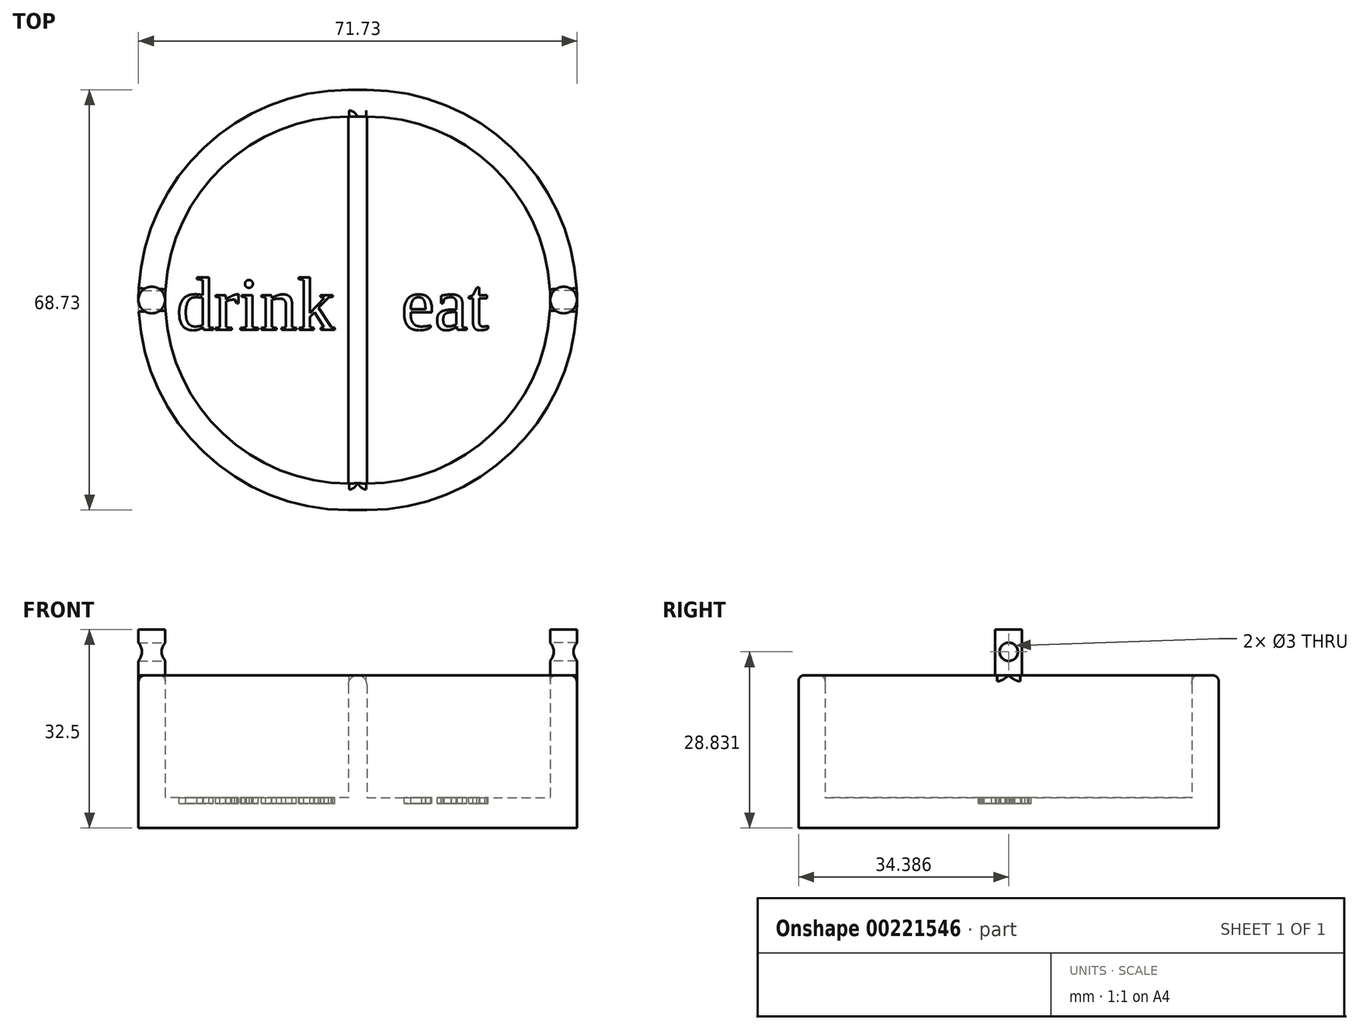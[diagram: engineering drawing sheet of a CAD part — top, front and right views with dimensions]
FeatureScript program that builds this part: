
annotation { "Feature Type Name" : "Feature", "Feature Type Description" : "" }
export const myFeature = defineFeature(function(context is Context, id is Id, definition is map)
    precondition{}
    {
        {
            var Q0;
            Q0=qCreatedBy(makeId("Top.planeOp"),FACE);
            var sketch = newSketch(context, id + "F0", { "sketchPlane" : qUnion([Q0])});
            skArc(sketch, "E0", {"start": v(1.15, 26.83) * mm, "mid": v(-28.85, -3.17) * mm, "end": v(1.15, -33.17) * mm});
            skArc(sketch, "E1", {"start": v(4.15, -33.17) * mm, "mid": v(34.15, -3.17) * mm, "end": v(4.15, 26.83) * mm});
            skLineSegment(sketch, "E2", {"start": v(1.15, 26.83) * mm, "end": v(4.15, 26.83) * mm});
            skLineSegment(sketch, "E3", {"start": v(1.15, -33.17) * mm, "end": v(4.15, -33.17) * mm});
            skArc(sketch, "E4", {"start": v(1.15, 31.2) * mm, "mid": v(-33.21, -3.17) * mm, "end": v(1.15, -37.54) * mm});
            skArc(sketch, "E5", {"start": v(4.15, -37.54) * mm, "mid": v(38.52, -3.17) * mm, "end": v(4.15, 31.2) * mm});
            skLineSegment(sketch, "E6", {"start": v(1.15, 31.2) * mm, "end": v(4.15, 31.2) * mm});
            skLineSegment(sketch, "E7", {"start": v(4.15, -37.54) * mm, "end": v(1.15, -37.54) * mm});
            skSolve(sketch);
        }
        {
            var Q0;
            Q0=makeQuery(id+"F0.imprint","IMPRINT",FACE,{"disambiguationData":[TD([[makeQuery(id+"F0.imprint","IMPRINT",EDGE,{"derivedFrom":sQuery(id+"F0.wireOp",EDGE,"E0")}),1.0]])]});
            var sketch = newSketch(context, id + "F1", { "sketchPlane" : qUnion([Q0])});
            skLineSegment(sketch, "E8", {"start": v(4.15, 26.83) * mm, "end": v(4.15, -33.17) * mm});
            skLineSegment(sketch, "E9", {"start": v(1.15, 26.83) * mm, "end": v(1.15, -33.17) * mm});
            skSolve(sketch);
        }
        {
            var Q0;
            Q0=qCreatedBy(makeId("Top.planeOp"),FACE);
            var sketch = newSketch(context, id + "F2", { "sketchPlane" : qUnion([Q0])});
            skLineSegment(sketch, "E10", {"start": v(1.15, 26.83) * mm, "end": v(4.15, 26.83) * mm});
            skLineSegment(sketch, "E11", {"start": v(4.15, 26.83) * mm, "end": v(4.15, -33.17) * mm});
            skLineSegment(sketch, "E12", {"start": v(4.15, -33.17) * mm, "end": v(1.15, -33.17) * mm});
            skLineSegment(sketch, "E13", {"start": v(1.15, -33.17) * mm, "end": v(1.15, 26.83) * mm});
            skSolve(sketch);
        }
        {
            var Q0;
            Q0=makeQuery(id+"F0.imprint","IMPRINT",FACE,{"disambiguationData":[TD([[makeQuery(id+"F0.imprint","IMPRINT",EDGE,{"derivedFrom":sQuery(id+"F0.wireOp",EDGE,"E0")}),-1.0]])]});
            extrude(context, id + "F3", {"entities" : qUnion([Q0]), "depth" : 25 * mm});
        }
        {
            var Q0;
            Q0=makeQuery(id+"F1.imprint","IMPRINT",FACE,{"disambiguationData":[TD([[makeQuery(id+"F1.imprint","IMPRINT",EDGE,{"derivedFrom":sQuery(id+"F1.wireOp",EDGE,"E9")}),-1.0]])]});
            var Q1;
            Q1=makeQuery(id+"F1.imprint","IMPRINT",FACE,{"disambiguationData":[TD([[makeQuery(id+"F1.imprint","IMPRINT",EDGE,{"derivedFrom":sQuery(id+"F1.wireOp",EDGE,"E8")}),1.0]])]});
            extrude(context, id + "F4", {"entities" : qUnion([Q0, Q1]), "operationType" : NewBodyOperationType.ADD, "depth" : 5 * mm});
        }
        {
            var Q0;
            Q0=makeQuery(id+"F2.imprint","IMPRINT",FACE,{"disambiguationData":[TD([[makeQuery(id+"F2.imprint","IMPRINT",EDGE,{"derivedFrom":sQuery(id+"F2.wireOp",EDGE,"E10")}),-1.0]])]});
            extrude(context, id + "F5", {"entities" : qUnion([Q0]), "operationType" : NewBodyOperationType.ADD, "depth" : 25 * mm});
        }
        {
            var Q0;
            Q0=makeQuery(id+"F5.opExtrude","CAP_EDGE",EDGE,{"disambiguationData":[OSD([sQuery(id+"F2.wireOp",EDGE,"E11")])],"isStart":false});
            var Q1;
            Q1=makeQuery(id+"F5.opExtrude","CAP_EDGE",EDGE,{"disambiguationData":[OSD([sQuery(id+"F2.wireOp",EDGE,"E13")])],"isStart":false});
            fillet(context, id + "F6", {"entities" : qUnion([Q0, Q1]), "radius" : 1.5 * mm, "tangentPropagation" : true, "allowEdgeOverflow" : false});
        }
        {
            var Q0;
            Q0=makeQuery(id+"F4.opExtrude","CAP_FACE",FACE,{"disambiguationData":[OSD([sQuery(id+"F0.wireOp",EDGE,"E1"),sQuery(id+"F1.wireOp",EDGE,"E8")])],"isStart":false});
            var sketch = newSketch(context, id + "F7", { "sketchPlane" : qUnion([Q0])});
            skText(sketch, "E14", { "text": "drink", "fontName": "Tinos-Regular.ttf"});
            skText(sketch, "E15", { "text": "eat", "fontName": "Tinos-Regular.ttf"});
            const initialGuessF7  = {"E14": [-0.02699, -0.00802, 1, 0, 0.00884], "E15": [0.00976, -0.00802, 1, 0, 0.00884]};
            skSetInitialGuess(sketch, initialGuessF7);
            skSolve(sketch);
        }
        {
            var Q0;
            Q0 = qSketchRegion(id + "F7", true);
            extrude(context, id + "F8", {"entities" : qUnion([Q0]), "operationType" : NewBodyOperationType.REMOVE, "oppositeDirection" : true, "depth" : 1 * mm});
        }
        {
            var Q0;
            Q0=makeQuery(id+"F5.boolean.opBoolean","MERGE",FACE,{"derivedFrom":[makeQuery(id+"F3.opExtrude","CAP_FACE",FACE,{"disambiguationData":[OSD([sQuery(id+"F0.wireOp",EDGE,"E0"),sQuery(id+"F0.wireOp",EDGE,"E1"),sQuery(id+"F0.wireOp",EDGE,"E2"),sQuery(id+"F0.wireOp",EDGE,"E3"),sQuery(id+"F0.wireOp",EDGE,"E4"),sQuery(id+"F0.wireOp",EDGE,"E5"),sQuery(id+"F0.wireOp",EDGE,"E6"),sQuery(id+"F0.wireOp",EDGE,"E7")])],"isStart":false}),makeQuery(id+"F5.opExtrude","CAP_FACE",FACE,{"disambiguationData":[OSD([sQuery(id+"F2.wireOp",EDGE,"E10"),sQuery(id+"F2.wireOp",EDGE,"E11"),sQuery(id+"F2.wireOp",EDGE,"E12"),sQuery(id+"F2.wireOp",EDGE,"E13")])],"isStart":false})]});
            var sketch = newSketch(context, id + "F9", { "sketchPlane" : qUnion([Q0])});
            skCircle(sketch, "E16", {"center": v(-31.03, -3.17) * mm, "radius": 2.18 * mm});
            skCircle(sketch, "E17", {"center": v(36.34, -3.17) * mm, "radius": 2.18 * mm});
            skSolve(sketch);
        }
        {
            var Q0;
            {var subQ0=sQuery(id+"F9.wireOp",EDGE,"E16");var subQ1=makeQuery(id+"F9.imprint","INTERSECT",VERTEX,{"derivedFrom":[makeQuery(id+"F3.opExtrude","CAP_EDGE",EDGE,{"disambiguationData":[OSD([sQuery(id+"F0.wireOp",EDGE,"E4")])],"isStart":false}),subQ0]});Q0=makeQuery(id+"F9.imprint","IMPRINT",FACE,{"disambiguationData":[TD([[makeQuery(id+"F9.imprint","IMPRINT",EDGE,{"disambiguationData":[TD([[subQ1,1.0]])],"derivedFrom":subQ0}),1.0]])]});}
            var Q1;
            {var subQ0=sQuery(id+"F9.wireOp",EDGE,"E17");var subQ1=makeQuery(id+"F9.imprint","INTERSECT",VERTEX,{"derivedFrom":[makeQuery(id+"F3.opExtrude","CAP_EDGE",EDGE,{"disambiguationData":[OSD([sQuery(id+"F0.wireOp",EDGE,"E5")])],"isStart":false}),subQ0]});Q1=makeQuery(id+"F9.imprint","IMPRINT",FACE,{"disambiguationData":[TD([[makeQuery(id+"F9.imprint","IMPRINT",EDGE,{"disambiguationData":[TD([[subQ1,-1.0]])],"derivedFrom":subQ0}),1.0]])]});}
            extrude(context, id + "F10", {"entities" : qUnion([Q0, Q1]), "operationType" : NewBodyOperationType.ADD, "depth" : 7.5 * mm});
        }
        {
            var Q0;
            Q0=qCreatedBy(makeId("Right.planeOp"),FACE);
            var sketch = newSketch(context, id + "F11", { "sketchPlane" : qUnion([Q0])});
            skCircle(sketch, "E18", {"center": v(-3.15, 28.83) * mm, "radius": 1.5 * mm});
            skSolve(sketch);
        }
        {
            var Q0;
            Q0=makeQuery(id+"F11.imprint","IMPRINT",FACE,{"disambiguationData":[TD([[makeQuery(id+"F11.imprint","IMPRINT",EDGE,{"derivedFrom":sQuery(id+"F11.wireOp",EDGE,"E18")}),1.0]])]});
            extrude(context, id + "F12", {"entities" : qUnion([Q0]), "operationType" : NewBodyOperationType.REMOVE, "oppositeDirection" : true, "depth" : 50 * mm});
        }
        {
            var Q0;
            Q0=qCreatedBy(makeId("Right.planeOp"),FACE);
            var sketch = newSketch(context, id + "F13", { "sketchPlane" : qUnion([Q0])});
            skCircle(sketch, "E19", {"center": v(-3.15, 28.83) * mm, "radius": 1.5 * mm});
            skSolve(sketch);
        }
        {
            var Q0;
            Q0=makeQuery(id+"F13.imprint","IMPRINT",FACE,{"disambiguationData":[TD([[makeQuery(id+"F13.imprint","IMPRINT",EDGE,{"derivedFrom":sQuery(id+"F13.wireOp",EDGE,"E19")}),1.0]])]});
            extrude(context, id + "F14", {"entities" : qUnion([Q0]), "operationType" : NewBodyOperationType.REMOVE, "depth" : 50 * mm});
        }
        {
            var Q0;
            Q0=makeQuery(id+"F10.boolean.opBoolean","SPLIT",EDGE,{"disambiguationData":[OD(0.0)],"derivedFrom":makeQuery(id+"F3.opExtrude","CAP_EDGE",EDGE,{"disambiguationData":[OSD([sQuery(id+"F0.wireOp",EDGE,"E1")])],"isStart":false})});
            var Q1;
            Q1=makeQuery(id+"F10.boolean.opBoolean","SPLIT",EDGE,{"disambiguationData":[OD(0.0)],"derivedFrom":makeQuery(id+"F3.opExtrude","CAP_EDGE",EDGE,{"disambiguationData":[OSD([sQuery(id+"F0.wireOp",EDGE,"E0")])],"isStart":false})});
            var Q2;
            Q2=makeQuery(id+"F10.boolean.opBoolean","SPLIT",EDGE,{"disambiguationData":[OD(1.0)],"derivedFrom":makeQuery(id+"F3.opExtrude","CAP_EDGE",EDGE,{"disambiguationData":[OSD([sQuery(id+"F0.wireOp",EDGE,"E0")])],"isStart":false})});
            var Q3;
            Q3=makeQuery(id+"F10.boolean.opBoolean","SPLIT",EDGE,{"disambiguationData":[OD(1.0)],"derivedFrom":makeQuery(id+"F3.opExtrude","CAP_EDGE",EDGE,{"disambiguationData":[OSD([sQuery(id+"F0.wireOp",EDGE,"E1")])],"isStart":false})});
            var Q4;
            {var subQ0=sQuery(id+"F0.wireOp",EDGE,"E7");var subQ1=sQuery(id+"F0.wireOp",EDGE,"E4");Q4=makeQuery(id+"F10.boolean.opBoolean","SPLIT",EDGE,{"disambiguationData":[TD([makeQuery(id+"F3.opExtrude","SWEPT_FACE",FACE,{"disambiguationData":[OSD([subQ0])]})])],"derivedFrom":makeQuery(id+"F3.opExtrude","CAP_EDGE",EDGE,{"disambiguationData":[OSD([subQ1])],"isStart":false})});}
            fillet(context, id + "F15", {"entities" : qUnion([Q0, Q1, Q2, Q3, Q4]), "radius" : 1 * mm, "tangentPropagation" : true, "allowEdgeOverflow" : false});
        }
    });
